# Revit family: FU_Chair_Sandler_Airy 2-1
name_source: partatom
category: Furniture
units: mm (PartAtom-declared; Revit-internal decimal feet)

## family parameters
Always vertical = Yes
Cut with Voids When Loaded = No
OmniClass Number = 23.40.20.00
OmniClass Title = General Furniture and Specialties
Render Appearance Source = Family Geometry
Room Calculation Point = No
Shared = No
Work Plane-Based = No

## types (1)
- Airy 2.1
    Default Elevation = 0 mm  [stored 0 ft]
    Depth = 530 mm  [stored 1.73885 ft]
    Description = Elegant armchair with an opening between the back and seat. Fluid backrest with integrated armrests, painted steel legs, and webbed seat for comfort.
    Height = 780 mm  [stored 2.55906 ft]
    Manufacturer = Sandler
    Model = Airy 2.1
    URL = https://www.sandlerseating.com
    Width = 620 mm  [stored 2.03412 ft]

note: [stored X ft] marks values corroborated as IEEE doubles in the binary element streams (Revit-internal decimal feet)

## geometry (parser evidence)
native form markers: Sweep x3
no freeform markers — native parametric forms only
